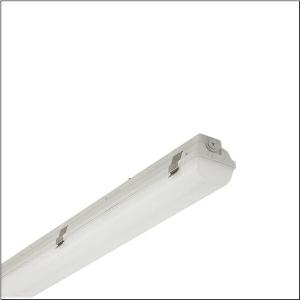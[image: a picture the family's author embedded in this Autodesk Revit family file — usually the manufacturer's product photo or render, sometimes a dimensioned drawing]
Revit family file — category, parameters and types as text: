
# Revit family: monsun_r__21_eco_51fj20dp47a_195a
name_source: partatom
category: Lighting Fixtures
units: mm (PartAtom-declared; Revit-internal decimal feet)

## family parameters
Cut with Voids When Loaded = No
Host = Face
Light Source = No
Part Type = Normal
Room Calculation Point = No
Round Connector Dimension = Use Diameter
Shared = No

## types (1)
- Monsun® 21 Eco (1 x LED, 6600 lm, 50 W, 4000K)
    Apparent Load = 50 VA
    CIE Flux Codes = 40 69 88 88 100
    Color Rendering = 80
    Color Temperature = 4000K
    Default Elevation = 1800 mm
    Description = Monsun® 21 Eco, damp-proof luminaire, primary optical cover: diffuser, of PC, UV-stabilised, frosted, light emission: direct distribution, primary light characteristic: symmetric, installation type: suspended mounting, surface-mounted, LED, rated luminous flux: 6.600lm, luminous efficacy: 132lm/W, light colour: 840, colour temperature: 4000K, control gear: ECG DALI, with terminal, 5-pole, max. 2.5mm², mains connection: 220..240V, AC, 50/60Hz, rated input power: 50W, housing, of glass-fibre reinforced polyester, light grey (RAL 7035), length: 1.577mm, width: 90mm, height: 95mm, clip for enclosure, of spring steel V2A, protection rating (complete): IP66, insulation class (complete): insulation class I (protective earthing), certification: CE, UKCA, protection symbol: D, impact resistance: IK08, permissible operating ambient temperature: -20..+35°C, corresponds to IFS (International Featured Standards) requirements for safety and quality in the food industry, contact your sales advisor before using the luminaires in applications with unclear chemical exposure, large temperature fluctuations or condensation-forming humidity, packaging unit: 1 piece
    Height = 103 mm
    Lamp = 1 x LED
    Lamp Light Flux = 6600 lm
    Lamp Power = 50 W
    Lamp count = 1
    Length = 1577 mm
    Luminous efficacy = 132 lm/W
    Manufacturer = Siteco
    ModVariant = No
    Model = 51FJ20DP47A
    Mounting Place = Ceiling
    Mounting Type = Surface mounted
    Number of Poles = 1
    OnlyDefault = Yes
    Power Factor = 1
    Product Name = Monsun® 21 Eco
    Product group = damp-proof luminaire
    ProductGroupID = 300
    Protection Class = Protection class I
    Protection Degree = IP 66
    RLX_Detail_Level = 1
    RLX_Emergency_Light_Flux = 0 lm
    RLX_Emergency_Type = 0
    RLX_Emergency_Type_DB = No
    RlxData = <blob elided: 33505 chars, md5=47855209>
    Socket = socket
    Standby Power = 0 W
    System Light Flux = 6600 lm
    System Power = 50 W
    Type Comments = Product without accessories
    Type Image = l_1007218.jpg
    URL = http://relux.com
    VarID = ---
    Voltage = 0 V
    Weight = 0.00 kg
    Width = 90 mm

## geometry (parser evidence)
native form markers: Blend x4, Sweep x12
no freeform markers — native parametric forms only
